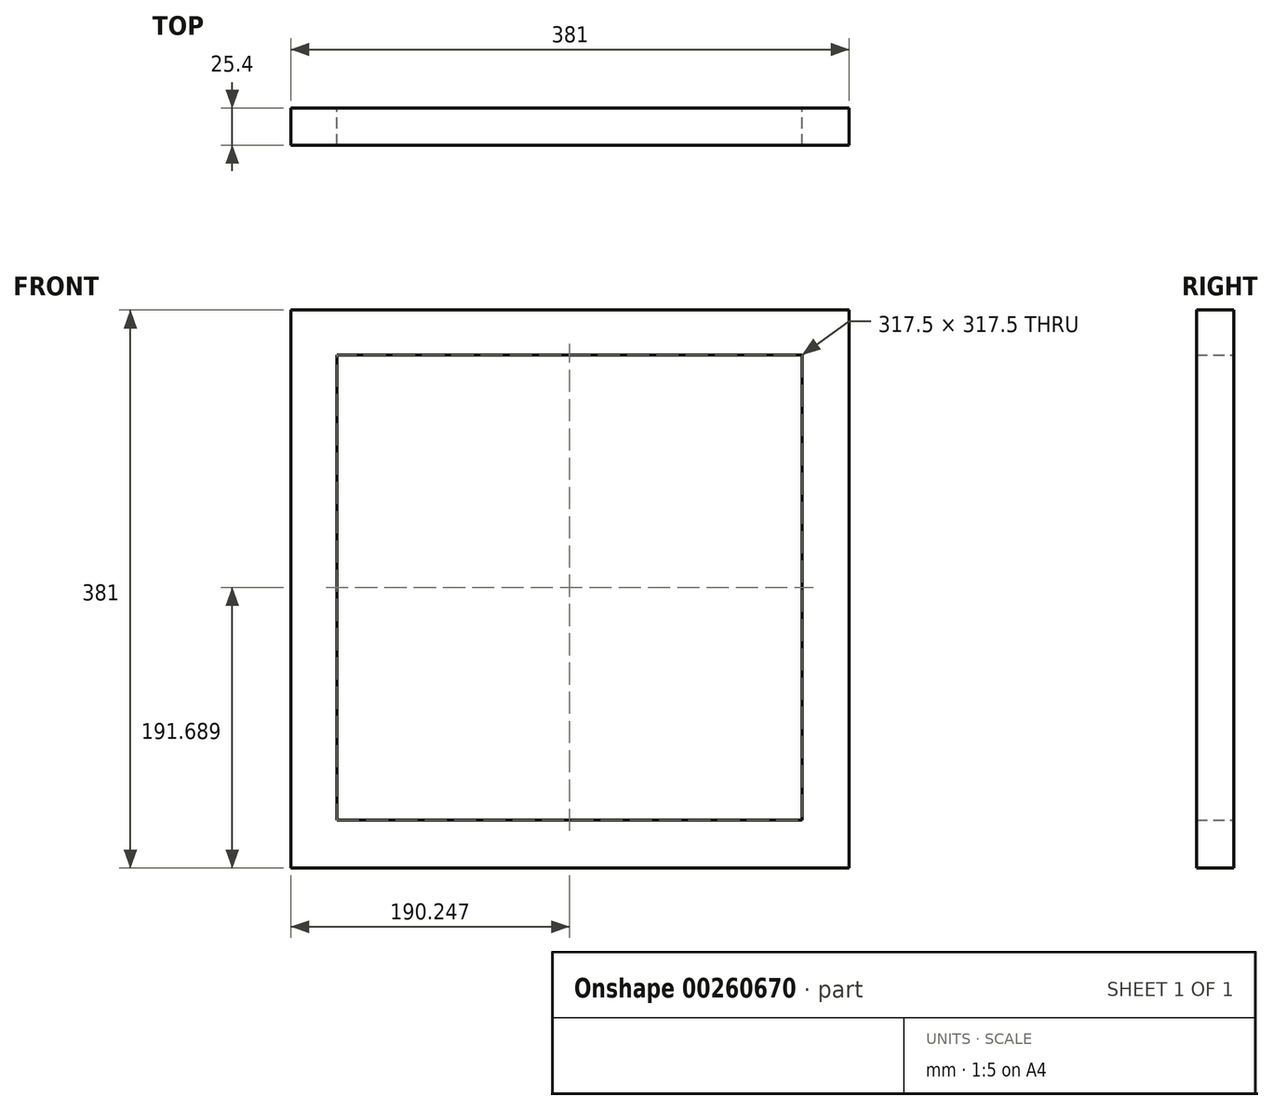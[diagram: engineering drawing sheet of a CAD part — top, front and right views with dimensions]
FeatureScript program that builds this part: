
annotation { "Feature Type Name" : "Feature", "Feature Type Description" : "" }
export const myFeature = defineFeature(function(context is Context, id is Id, definition is map)
    precondition{}
    {
        {
            var Q0;
            Q0=qCreatedBy(makeId("Front.planeOp"),FACE);
            var sketch = newSketch(context, id + "F0", { "sketchPlane" : qUnion([Q0])});
            skLineSegment(sketch, "E0.bottom", {"start": v(-198.48, 195.88) * mm, "end": v(182.52, 195.88) * mm});
            skLineSegment(sketch, "E0.top", {"start": v(-198.48, -185.12) * mm, "end": v(182.52, -185.12) * mm});
            skLineSegment(sketch, "E0.left", {"start": v(-198.48, 195.88) * mm, "end": v(-198.48, -185.12) * mm});
            skLineSegment(sketch, "E0.right", {"start": v(182.52, 195.88) * mm, "end": v(182.52, -185.12) * mm});
            skLineSegment(sketch, "E1.bottom", {"start": v(-166.98, 165.32) * mm, "end": v(150.52, 165.32) * mm});
            skLineSegment(sketch, "E1.top", {"start": v(-166.98, -152.18) * mm, "end": v(150.52, -152.18) * mm});
            skLineSegment(sketch, "E1.left", {"start": v(-166.98, 165.32) * mm, "end": v(-166.98, -152.18) * mm});
            skLineSegment(sketch, "E1.right", {"start": v(150.52, 165.32) * mm, "end": v(150.52, -152.18) * mm});
            skSolve(sketch);
        }
        {
            var Q0;
            Q0 = qSketchRegion(id + "F0", true);
            extrude(context, id + "F1", {"entities" : qUnion([Q0]), "depth" : 25.4 * mm});
        }
    });
